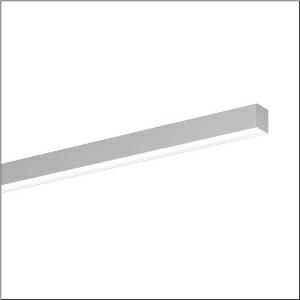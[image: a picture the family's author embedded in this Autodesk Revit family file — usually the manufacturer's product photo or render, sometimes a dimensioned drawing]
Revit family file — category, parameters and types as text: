
# Revit family: silica_r__21_51mx20tat2s_7558
name_source: partatom
category: Lighting Fixtures
units: mm (PartAtom-declared; Revit-internal decimal feet)

## family parameters
Cut with Voids When Loaded = No
Host = Face
Light Source = No
Part Type = Normal
Room Calculation Point = No
Round Connector Dimension = Use Diameter
Shared = No

## types (1)
- --- (1 x LED, 2400 lm, 20.5 W, 6500K)
    Apparent Load = 21 VA
    CIE Flux Codes = 48 79 96 100 100
    Color Rendering = 80
    Color Temperature = 6500K
    Default Elevation = 1800 mm
    Description = Silica® 21, office luminaire, primary optical cover: cover, of PMMA, opal, light emission: direct distribution, primary light characteristic: symmetric, installation type: surface-mounted, LED, rated luminous flux: 2.400lm, luminous efficacy: 112lm/W, light colour: 8tw, colour temperature: 2700..6500K, control gear: DALI DT8, with terminal, 3+2-pole, max. 2.5mm², mains connection: 220..240V, AC, 50/60Hz, rated input power: 21.5W, luminaire housing, of aluminium, metallic grey (RAL 9006), length: 1.204mm, width: 53mm, height: 53mm, protection rating (complete): IP20, insulation class (complete): insulation class I (protective earthing), certification: CE, permissible operating ambient temperature: 0..+35°C, standard: EN 50419, packaging unit: 1 piece
    Height = 53 mm
    Lamp = 1 x LED
    Lamp Light Flux = 2400 lm
    Lamp Power = 20.5 W
    Lamp count = 1
    Length = 1204 mm
    Luminous efficacy = 117 lm/W
    Manufacturer = Siteco
    ModVariant = No
    Model = 51MX20TAT2S
    Mounting Place = Ceiling
    Mounting Type = Surface mounted
    Number of Poles = 1
    OnlyDefault = Yes
    Power Factor = 1
    Product Name = Silica® 21
    Product group = office luminaire | ceiling mounted
    ProductGroupID = 302
    Protection Class = Protection class I
    Protection Degree = IP 20
    RLX_Detail_Level = 1
    RLX_Emergency_Light_Flux = 0 lm
    RLX_Emergency_Type = 0
    RLX_Emergency_Type_DB = No
    RlxData = <blob elided: 23153 chars, md5=fb6cc15d>
    Socket = socket
    Standby Power = 0 W
    System Light Flux = 2400 lm
    System Power = 21 W
    Type Comments = individual setting
    Type Image = l_1335933.jpg
    URL = http://relux.com
    VarID = @adj_139674
    Voltage = 0 V
    Weight = 0.00 kg
    Width = 53 mm

## geometry (parser evidence)
native form markers: Blend x4, Sweep x9
no freeform markers — native parametric forms only
